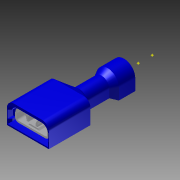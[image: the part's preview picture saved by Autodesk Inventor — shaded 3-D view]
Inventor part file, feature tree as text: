
AUTODESK INVENTOR PART (.ipt)
format: ipt  version: 2011 (Build 150239000, 239)  size: 261,632 bytes
history: native  units: in
note: dims shown in document units (in); Inventor stores cm internally (conversion verified against a paired STEP export)
features: other x4, plane x2, imported_body x1, sketch x1
ambient origin geometry x8: Origin, YZ Plane, XZ Plane, XY Plane, X Axis, Y Axis, Z Axis, Center Point
bodies: Solid1 (feature_tree)
feature tree (8):
  imported_body  "Base1"
  sketch  "Sketch1"  dims[d0=0.125in d1=0.25in]
  other  "Work Point2"
  other  "Work Point3"
  plane  "Work Plane1"
  other  "Work Axis1"
  plane  "Work Plane2"
  other  "Work Axis2"
